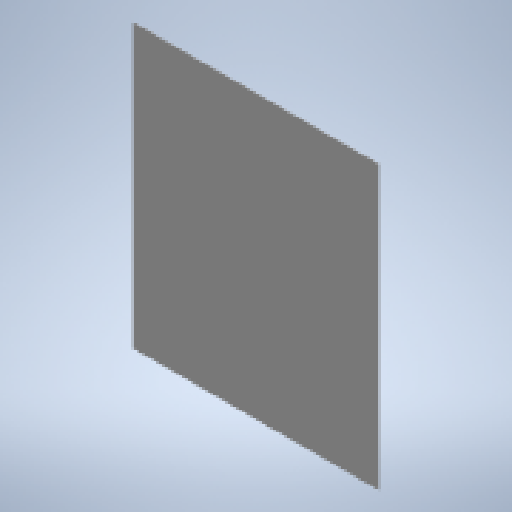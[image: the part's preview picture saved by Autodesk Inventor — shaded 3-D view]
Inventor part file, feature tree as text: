
AUTODESK INVENTOR PART (.ipt)
format: ipt  version: 2023 (Build 270158000, 158)  size: 119,808 bytes
history: native  units: in
note: dims shown in document units (in); Inventor stores cm internally (conversion verified against a paired STEP export)
features: extrude x1, sketch x1
ambient origin geometry x8: Origin, YZ Plane, XZ Plane, XY Plane, X Axis, Y Axis, Z Axis, Center Point
bodies: Solid1 (feature_tree)
feature tree (2):
  extrude  "Extrusion1"  Depth=48.0in
  sketch  "Sketch1"  dims[d0=53.0in d1=48.0in d2=0.1in d3=0.0in]
